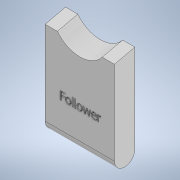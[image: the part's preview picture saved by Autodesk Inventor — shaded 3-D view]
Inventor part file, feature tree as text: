
AUTODESK INVENTOR PART (.ipt)
format: ipt  version: 2021 (Build 250183000, 183)  size: 257,536 bytes
history: native  units: mm
features: sketch x5, extrude x2, fillet x1, plane x1, sweep x1, emboss x1
ambient origin geometry x8: Origin, YZ Plane, XZ Plane, XY Plane, X Axis, Y Axis, Z Axis, Center Point
bodies: Solid1 (feature_tree)
feature tree (11):
  extrude  "Extrusion1"  Depth=24.25mm
  fillet  "Fillet2"  Radius=5.0mm
  plane  "Work Plane1"
  sweep  "Sweep1"
  extrude  "Extrusion6"  TaperAngle=0.0deg  [1 undecoded]
  emboss  "Emboss1"
  sketch  "Sketch1"  dims[d0=17.0mm d1=24.25mm d2=5.0mm d3=0.0mm]
  sketch  "Sketch5"  dims[d15=2.5mm d21=-8.5mm]
  sketch  "Sketch6"  dims[d22=2.268928mm d25=0.0mm d26=0.0mm]
  sketch  "Sketch8"  dims[d27=3.0mm]
  sketch  "Sketch9"  dims[d31=3.0mm d32=3.0mm d33=3.0mm d34=7.0mm d35=17.0mm d36=0.0mm d37=1.0mm d38=0.0mm d16=0.872665mm d17=0.5mm d18=0.872665mm]
note: 1 required parameter value undecoded (feature->parameter linkage not recoverable at this tier; creation-order binding heuristic only, values carry confidence <= 0.55)
